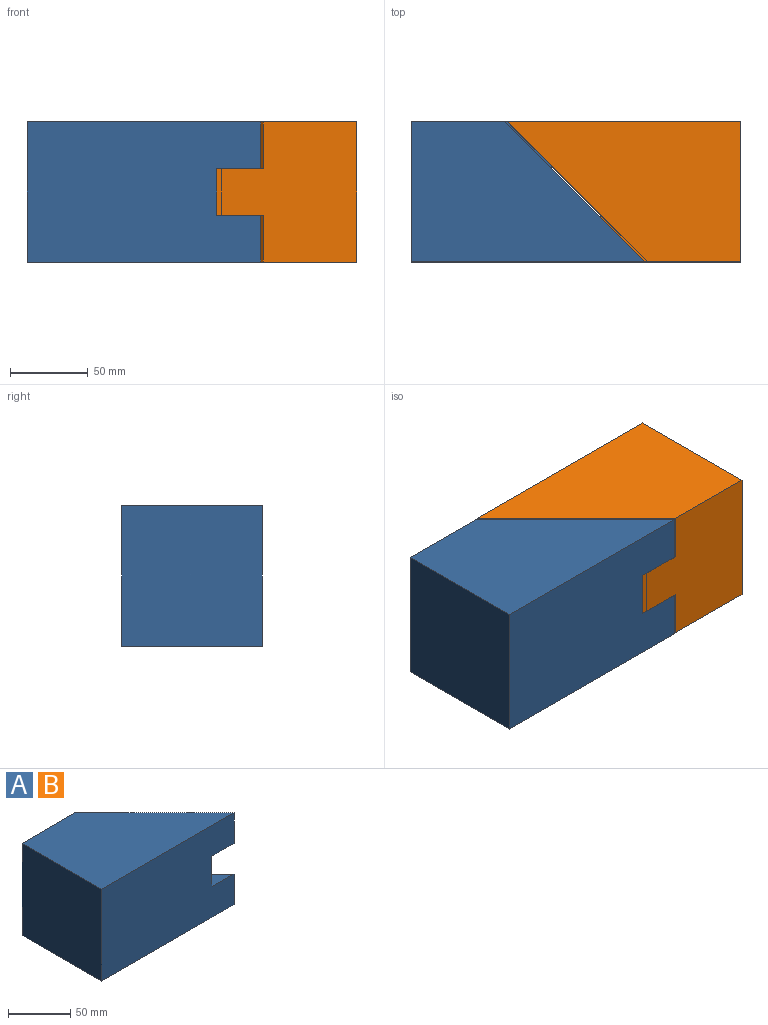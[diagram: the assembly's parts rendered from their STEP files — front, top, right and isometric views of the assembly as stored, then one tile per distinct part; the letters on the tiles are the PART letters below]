
ASSEMBLY  parts=2 mates=1
PART A: 12 faces, bbox 150x90x90 mm
  f0: plane 90x90mm, normal (0.71,0.71,0), area 9121.7mm2, adj f1,f3,f4,f5,f6,f7,f8,f9
  f1: plane 150x90mm, normal (0,-1,0), area 12750mm2, adj f0,f2,f4,f5,f9,f10,f11
  f2: plane 90x90mm, normal (-1,0,0), area 8100mm2, adj f1,f3,f4,f5
  f3: plane 90x90mm, normal (0,1,0), area 6300mm2, adj f0,f2,f4,f5,f6,f7,f8
  f4: plane 150x90mm, normal (0,0,1), area 9450mm2, adj f0,f1,f2,f3
  f5: plane 150x90mm, normal (0,0,-1), area 9450mm2, adj f0,f1,f2,f3
  f6: plane 30x30mm, normal (0,0,1), area 450mm2, adj f0,f3,f8
  f7: plane 30x30mm, normal (0,0,-1), area 450mm2, adj f0,f3,f8
  f8: plane 30x30mm, normal (1,0,0), area 900mm2, adj f0,f3,f6,f7
  f9: plane 25x25mm, normal (0,0,-1), area 312.5mm2, adj f0,f1,f11
  f10: plane 25x25mm, normal (0,0,1), area 312.5mm2, adj f0,f1,f11
  f11: plane 30x25mm, normal (1,0,0), area 750mm2, adj f0,f1,f9,f10
PART B: same geometry as A
PLACE A t=(4.04,-9.91,0)mm
PLACE B rot(axis=(0,0,-1),180deg) t=(215.79,80.09,0)mm
MATE planar A.f3 <-> B.f1  axis (0,1,0) through (40.47,80.09,45)mm
